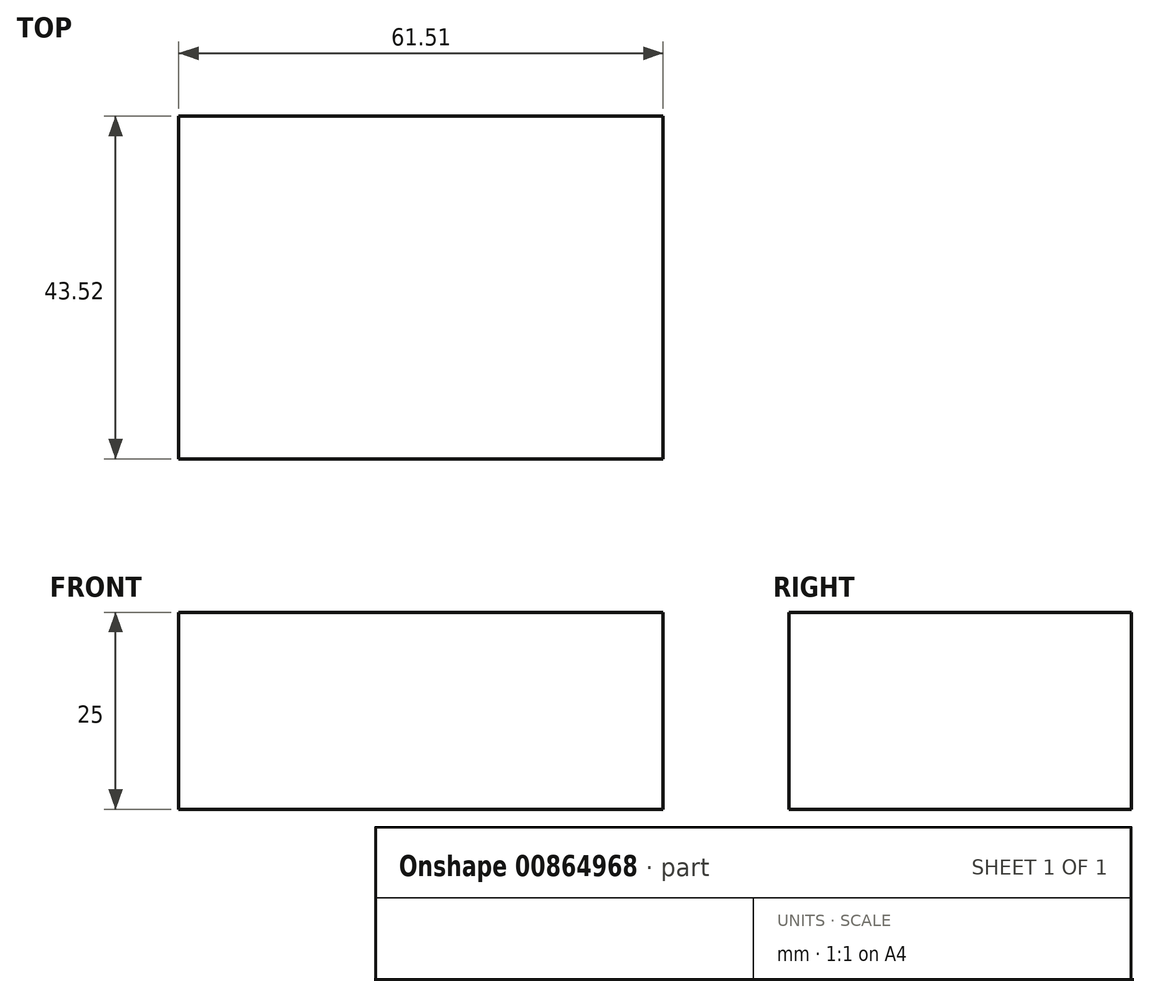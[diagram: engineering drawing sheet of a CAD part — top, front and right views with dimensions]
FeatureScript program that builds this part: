
annotation { "Feature Type Name" : "Feature", "Feature Type Description" : "" }
export const myFeature = defineFeature(function(context is Context, id is Id, definition is map)
    precondition{}
    {
        {
            var Q0;
            Q0=qCreatedBy(makeId("Top.planeOp"),FACE);
            var sketch = newSketch(context, id + "F0", { "sketchPlane" : qUnion([Q0])});
            skLineSegment(sketch, "E0.bottom", {"start": v(-29.68, 19.05) * mm, "end": v(31.83, 19.05) * mm});
            skLineSegment(sketch, "E0.top", {"start": v(-29.68, -24.47) * mm, "end": v(31.83, -24.47) * mm});
            skLineSegment(sketch, "E0.left", {"start": v(-29.68, 19.05) * mm, "end": v(-29.68, -24.47) * mm});
            skLineSegment(sketch, "E0.right", {"start": v(31.83, 19.05) * mm, "end": v(31.83, -24.47) * mm});
            skSolve(sketch);
        }
        {
            var Q0;
            Q0 = qSketchRegion(id + "F0", true);
            extrude(context, id + "F1", {"entities" : qUnion([Q0]), "depth" : 25 * mm, "offsetDistance" : 25 * mm});
        }
    });
